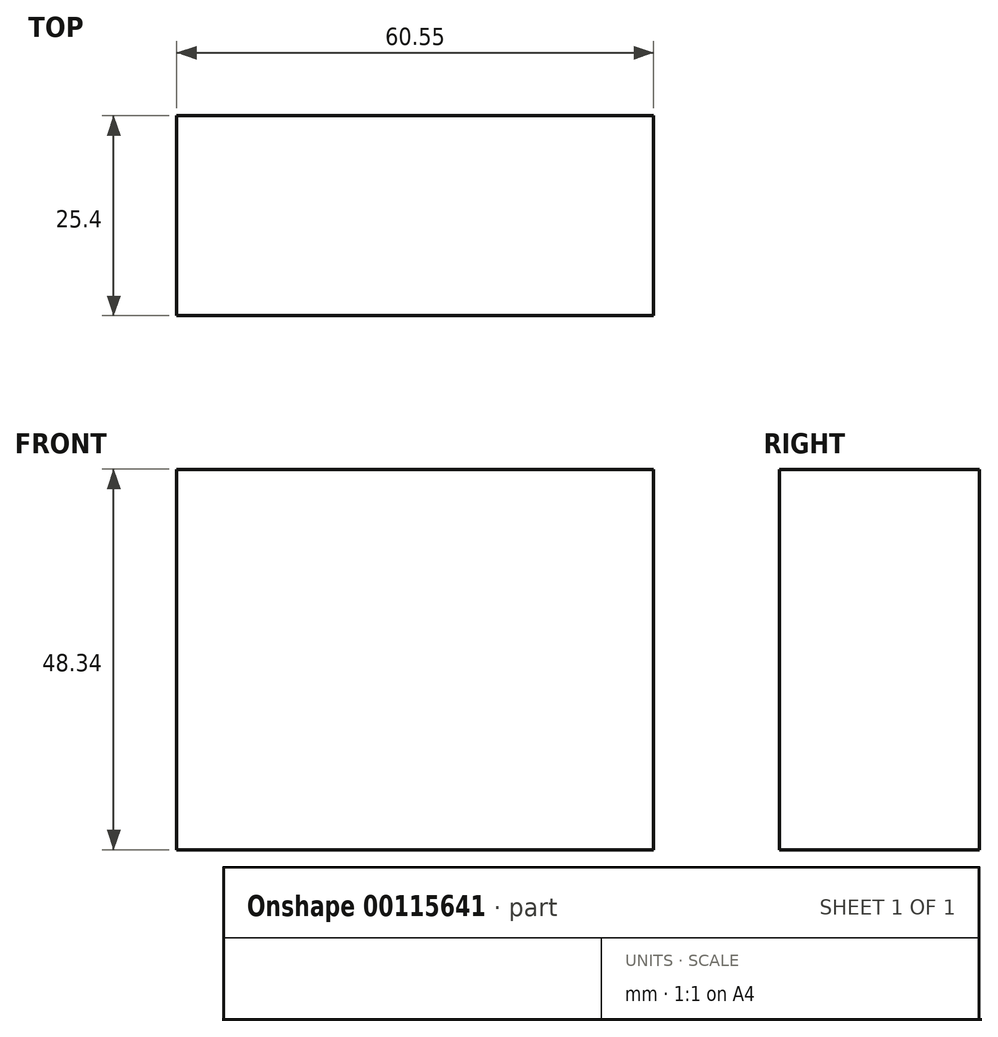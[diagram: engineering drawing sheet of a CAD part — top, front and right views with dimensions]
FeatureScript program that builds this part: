
annotation { "Feature Type Name" : "Feature", "Feature Type Description" : "" }
export const myFeature = defineFeature(function(context is Context, id is Id, definition is map)
    precondition{}
    {
        {
            var Q0;
            Q0=qCreatedBy(makeId("Front.planeOp"),FACE);
            var sketch = newSketch(context, id + "F0", { "sketchPlane" : qUnion([Q0])});
            skLineSegment(sketch, "E0.bottom", {"start": v(-120.73, 31.16) * mm, "end": v(-60.18, 31.16) * mm});
            skLineSegment(sketch, "E0.top", {"start": v(-120.73, -17.18) * mm, "end": v(-60.18, -17.18) * mm});
            skLineSegment(sketch, "E0.left", {"start": v(-120.73, 31.16) * mm, "end": v(-120.73, -17.18) * mm});
            skLineSegment(sketch, "E0.right", {"start": v(-60.18, 31.16) * mm, "end": v(-60.18, -17.18) * mm});
            skSolve(sketch);
        }
        {
            var Q0;
            Q0=makeQuery(id+"F0.imprint","IMPRINT",FACE,{"disambiguationData":[TD([[makeQuery(id+"F0.imprint","IMPRINT",EDGE,{"derivedFrom":sQuery(id+"F0.wireOp",EDGE,"E0.bottom")}),-1.0]])]});
            extrude(context, id + "F1", {"entities" : qUnion([Q0]), "depth" : 25.4 * mm});
        }
    });
